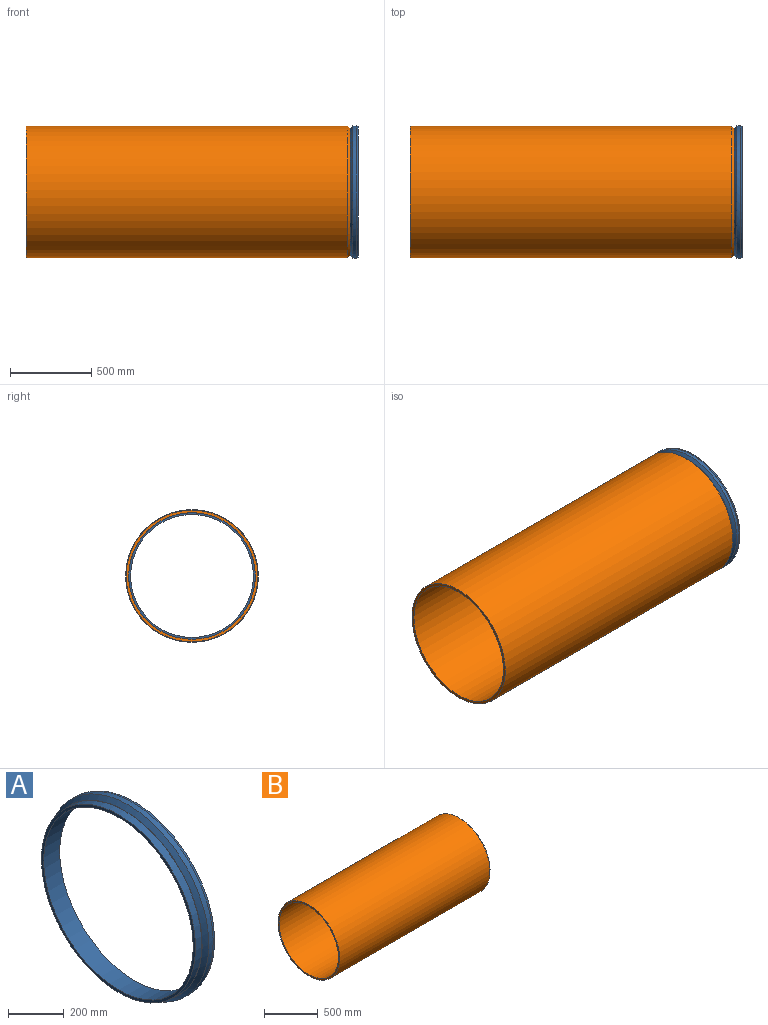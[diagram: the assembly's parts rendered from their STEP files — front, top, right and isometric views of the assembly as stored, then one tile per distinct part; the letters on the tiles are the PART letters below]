
ASSEMBLY  parts=2 mates=1
PART A: 9 faces, bbox 81x818x818 mm
  f0: cylinder r=409mm len=818mm, axis (1,0,0), area 56536.1mm2, adj f5,f8
  f1: plane 781x781mm, normal (-1,0,0), area 27800.7mm2, adj f3,f6
  f2: plane 812x812mm, normal (1,0,0), area 66586.1mm2, adj f3,f4
  f3: cylinder r=379mm len=758mm, axis (1,0,0), area 192887.5mm2, adj f1,f2
  f4: cylinder r=406mm len=812mm, axis (1,0,0), area 25509.7mm2, adj f2,f5
  f5: plane 818x818mm, normal (1,0,0), area 7681.2mm2, adj f0,f4
  f6: cylinder r=390.5mm len=781mm, axis (-1,0,0), area 78514.7mm2, adj f1,f7
  f7: plane 784x784mm, normal (-1,0,0), area 3687.4mm2, adj f6,f8
  f8: cone r=409mm half-angle=45deg, axis (1,0,0), area 60498.7mm2, adj f0,f7
PART B: 5 faces, bbox 2000x813x813 mm
  f0: cylinder r=390.5mm len=2000mm, axis (1,0,0), area 4907167.7mm2, adj f2,f3
  f1: cylinder r=406.5mm len=1986mm, axis (1,0,0), area 5072472mm2, adj f2,f4
  f2: plane 813x813mm, normal (-1,0,0), area 40061.6mm2, adj f0,f1
  f3: plane 785x785mm, normal (1,0,0), area 4919.7mm2, adj f0,f4
  f4: cone r=392.5mm half-angle=45deg, axis (-1,0,0), area 49698.1mm2, adj f1,f3
PLACE A t=(-1315.91,-440.8,471.07)mm
PLACE B t=(-864.91,-440.8,471.07)mm
MATE fastened A.f3 <-> B.f0  axis (1,0,0) through (-1815.91,-440.8,471.07)mm
